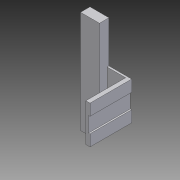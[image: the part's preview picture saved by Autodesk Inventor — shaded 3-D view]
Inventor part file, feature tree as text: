
AUTODESK INVENTOR PART (.ipt)
format: ipt  version: 2011 (Build 150239000, 239)  size: 93,184 bytes
history: native  units: in
note: dims shown in document units (in); Inventor stores cm internally (conversion verified against a paired STEP export)
features: other x1, imported_body x1, extrude x1, sketch x1
ambient origin geometry x8: Origin, YZ Plane, XZ Plane, XY Plane, X Axis, Y Axis, Z Axis, Center Point
feature tree (4):
  other  "Part2"
  imported_body  "Base1"
  extrude  "Extrusion1"  [1 undecoded]
  sketch  "Sketch1"  dims[d0=0.3937in d1=0.0in]
note: 1 required parameter value undecoded (feature->parameter linkage not recoverable at this tier; creation-order binding heuristic only, values carry confidence <= 0.55)
